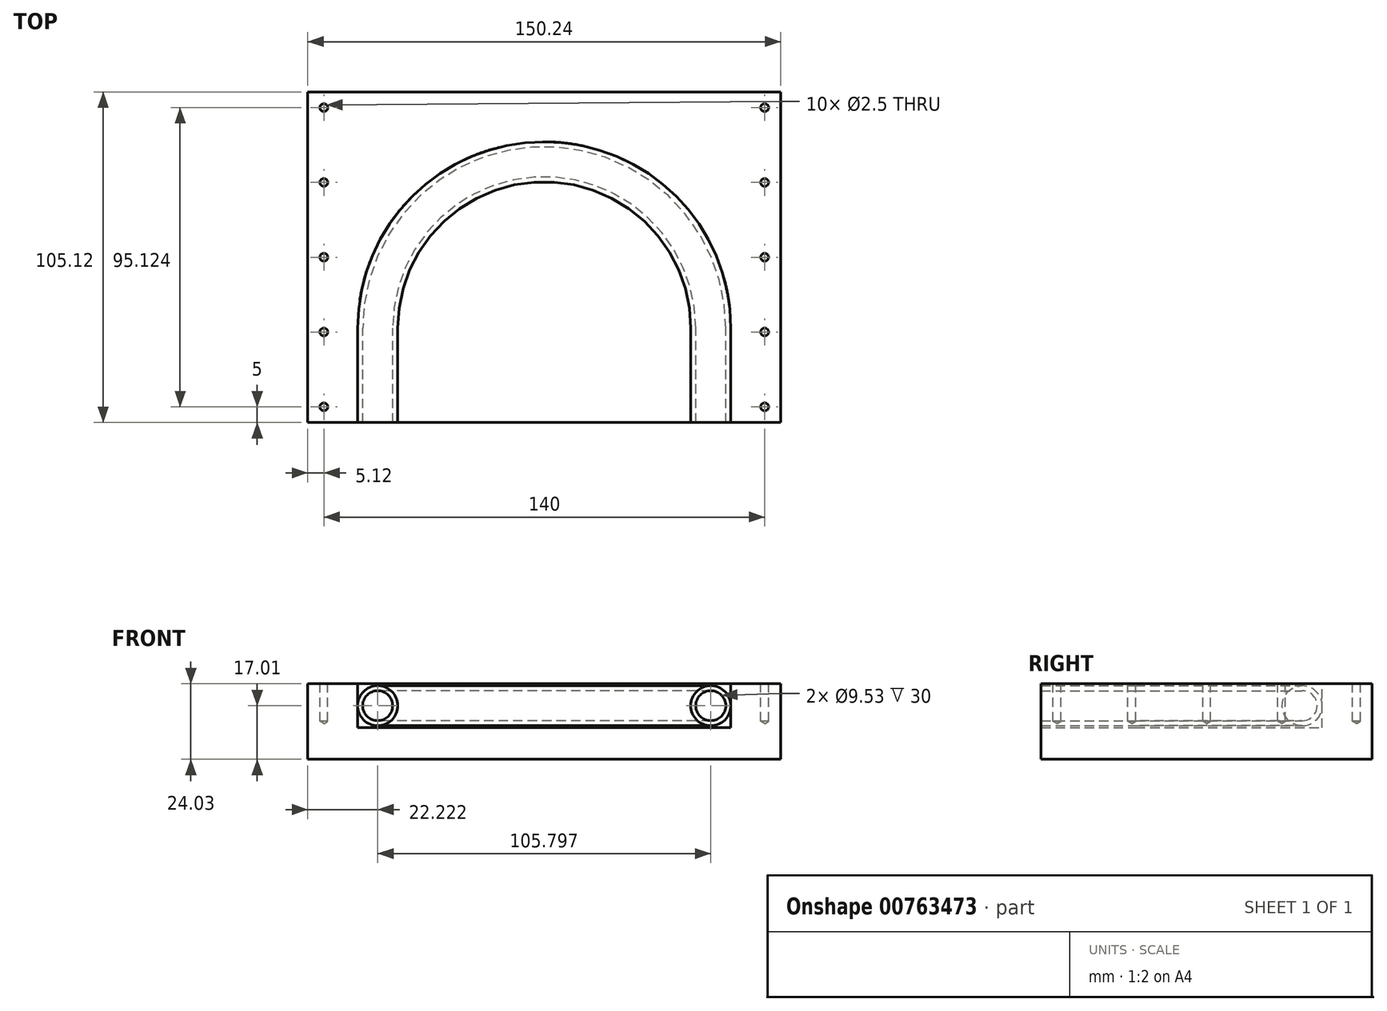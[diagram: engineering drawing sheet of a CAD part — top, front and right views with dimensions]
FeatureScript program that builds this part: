
annotation { "Feature Type Name" : "Feature", "Feature Type Description" : "" }
export const myFeature = defineFeature(function(context is Context, id is Id, definition is map)
    precondition{}
    {
        {
            var Q0;
            Q0=qCreatedBy(makeId("Right.planeOp"),FACE);
            var sketch = newSketch(context, id + "F0", { "sketchPlane" : qUnion([Q0])});
            skCircle(sketch, "E0", {"center": v(52.9, 0) * mm, "radius": 4.76 * mm});
            skCircle(sketch, "E1", {"center": v(52.9, 0) * mm, "radius": 6.35 * mm});
            skLineSegment(sketch, "E2", {"start": v(0, 42.85) * mm, "end": v(0, -34.67) * mm, "construction": true});
            skLineSegment(sketch, "E3.bottom", {"start": v(59.25, 7.01) * mm, "end": v(65.12, 7.01) * mm});
            skLineSegment(sketch, "E3.top", {"start": v(59.25, -7.01) * mm, "end": v(65.12, -7.01) * mm});
            skLineSegment(sketch, "E3.left", {"start": v(59.25, 7.01) * mm, "end": v(59.25, -7.01) * mm});
            skLineSegment(sketch, "E3.right", {"start": v(65.12, 7.01) * mm, "end": v(65.12, -7.01) * mm});
            skPoint(sketch, "E3.middle", {"position": v(62.19, 0) * mm});
            skPoint(sketch, "E4.visualSharp", {"position": v(59.25, 7.01) * mm});
            skPoint(sketch, "E5.visualSharp", {"position": v(65.12, 7.01) * mm});
            skLineSegment(sketch, "E6.bottom", {"start": v(65.12, -7.01) * mm, "end": v(-30, -7.01) * mm});
            skLineSegment(sketch, "E6.top", {"start": v(65.12, -17.01) * mm, "end": v(-30, -17.01) * mm});
            skLineSegment(sketch, "E6.left", {"start": v(65.12, -7.01) * mm, "end": v(65.12, -17.01) * mm});
            skLineSegment(sketch, "E6.right", {"start": v(-30, -7.01) * mm, "end": v(-30, -17.01) * mm});
            skSolve(sketch);
        }
        {
            var Q0;
            Q0=makeQuery(id+"F0.imprint","IMPRINT",FACE,{"disambiguationData":[TD([[makeQuery(id+"F0.imprint","IMPRINT",EDGE,{"derivedFrom":sQuery(id+"F0.wireOp",EDGE,"E0")}),-1.0]])]});
            var Q1;
            Q1=sQuery(id+"F0.wireOp",EDGE,"E2");
            revolve(context, id + "F1", {"surfaceOperationType" : NewSurfaceOperationType.NEW, "entities" : qUnion([Q0]), "axis" : qUnion([Q1]), "revolveType" : RevolveType.SYMMETRIC, "angle" : 180 * degree});
        }
        {
            var Q0;
            Q0=makeQuery(id+"F0.imprint","IMPRINT",FACE,{"disambiguationData":[TD([[makeQuery(id+"F0.imprint","IMPRINT",EDGE,{"derivedFrom":sQuery(id+"F0.wireOp",EDGE,"E3.bottom")}),-1.0]])]});
            var Q1;
            Q1=sQuery(id+"F0.wireOp",EDGE,"E2");
            revolve(context, id + "F2", {"operationType" : NewBodyOperationType.ADD, "surfaceOperationType" : NewSurfaceOperationType.NEW, "entities" : qUnion([Q0]), "axis" : qUnion([Q1]), "revolveType" : RevolveType.SYMMETRIC, "angle" : 180 * degree});
        }
        {
            var Q0;
            Q0=makeQuery(id+"F2.opRevolve","CAP_FACE",FACE,{"disambiguationData":[OSD([sQuery(id+"F0.wireOp",EDGE,"E3.bottom"),sQuery(id+"F0.wireOp",EDGE,"E3.top"),sQuery(id+"F0.wireOp",EDGE,"E3.left"),sQuery(id+"F0.wireOp",EDGE,"E3.right"),sQuery(id+"F0.wireOp",EDGE,"E4.filletArc"),sQuery(id+"F0.wireOp",EDGE,"E5.filletArc")])],"isStart":true});
            var Q1;
            Q1=makeQuery(id+"F2.opRevolve","CAP_FACE",FACE,{"disambiguationData":[OSD([sQuery(id+"F0.wireOp",EDGE,"E3.bottom"),sQuery(id+"F0.wireOp",EDGE,"E3.top"),sQuery(id+"F0.wireOp",EDGE,"E3.left"),sQuery(id+"F0.wireOp",EDGE,"E3.right"),sQuery(id+"F0.wireOp",EDGE,"E4.filletArc"),sQuery(id+"F0.wireOp",EDGE,"E5.filletArc")])],"isStart":false});
            extrude(context, id + "F3", {"entities" : qUnion([Q0, Q1]), "operationType" : NewBodyOperationType.ADD, "depth" : 30 * mm, "offsetDistance" : 25 * mm});
        }
        {
            var Q0;
            Q0=makeQuery(id+"F1.opRevolve","CAP_FACE",FACE,{"disambiguationData":[OSD([sQuery(id+"F0.wireOp",EDGE,"E0"),sQuery(id+"F0.wireOp",EDGE,"E1")])],"isStart":true});
            var Q1;
            Q1=makeQuery(id+"F1.opRevolve","CAP_FACE",FACE,{"disambiguationData":[OSD([sQuery(id+"F0.wireOp",EDGE,"E0"),sQuery(id+"F0.wireOp",EDGE,"E1")])],"isStart":false});
            extrude(context, id + "F4", {"entities" : qUnion([Q0, Q1]), "operationType" : NewBodyOperationType.ADD, "depth" : 30 * mm, "offsetDistance" : 25 * mm});
        }
        {
            var Q0;
            Q0=qCreatedBy(makeId("Top.planeOp"),FACE);
            var sketch = newSketch(context, id + "F5", { "sketchPlane" : qUnion([Q0])});
            skLineSegment(sketch, "E7.bottom", {"start": v(52.5, -3.17) * mm, "end": v(-52.5, -3.17) * mm});
            skLineSegment(sketch, "E7.top", {"start": v(52.5, 3.17) * mm, "end": v(-52.5, 3.17) * mm});
            skLineSegment(sketch, "E7.left", {"start": v(52.5, -3.18) * mm, "end": v(52.5, 3.18) * mm});
            skLineSegment(sketch, "E7.right", {"start": v(-52.5, -3.17) * mm, "end": v(-52.5, 3.17) * mm});
            skPoint(sketch, "E7.middle", {"position": v(0, 0) * mm});
            skArc(sketch, "E8", {"start": v(-52.5, 3.17) * mm, "mid": v(-55.67, 0) * mm, "end": v(-52.5, -3.17) * mm});
            skArc(sketch, "E9", {"start": v(52.5, -3.18) * mm, "mid": v(55.68, 0) * mm, "end": v(52.5, 3.18) * mm});
            skCircle(sketch, "E10", {"center": v(0, 0) * mm, "radius": 1.47 * mm});
            skSolve(sketch);
        }
        {
            var Q0;
            Q0=makeQuery(id+"F0.imprint","IMPRINT",FACE,{"disambiguationData":[TD([[makeQuery(id+"F0.imprint","IMPRINT",EDGE,{"derivedFrom":sQuery(id+"F0.wireOp",EDGE,"E6.top")}),-1.0]])]});
            extrude(context, id + "F6", {"entities" : qUnion([Q0]), "operationType" : NewBodyOperationType.ADD, "endBound" : BoundingType.SYMMETRIC, "depth" : 150.24 * mm, "offsetDistance" : 25 * mm});
        }
        {
            var Q0;
            Q0=makeQuery(id+"F5.imprint","IMPRINT",FACE,{"disambiguationData":[TD([[makeQuery(id+"F5.imprint","IMPRINT",EDGE,{"derivedFrom":sQuery(id+"F5.wireOp",EDGE,"E7.bottom")}),-1.0]])]});
            var Q1;
            {var subQ0=sQuery(id+"F5.wireOp",EDGE,"E7.left");Q1=makeQuery(id+"F5.imprint","IMPRINT",FACE,{"disambiguationData":[TD([[makeQuery(id+"F5.imprint","IMPRINT",EDGE,{"derivedFrom":subQ0}),-1.0]])]});}
            var Q2;
            {var subQ0=sQuery(id+"F5.wireOp",EDGE,"E7.left");Q2=makeQuery(id+"F5.imprint","IMPRINT",FACE,{"disambiguationData":[TD([[makeQuery(id+"F5.imprint","IMPRINT",EDGE,{"derivedFrom":subQ0}),1.0]])]});}
            var Q3;
            {var subQ0=sQuery(id+"F5.wireOp",EDGE,"E7.right");Q3=makeQuery(id+"F5.imprint","IMPRINT",FACE,{"disambiguationData":[TD([[makeQuery(id+"F5.imprint","IMPRINT",EDGE,{"derivedFrom":subQ0}),1.0]])]});}
            var Q4;
            {var subQ0=sQuery(id+"F5.wireOp",EDGE,"E7.right");Q4=makeQuery(id+"F5.imprint","IMPRINT",FACE,{"disambiguationData":[TD([[makeQuery(id+"F5.imprint","IMPRINT",EDGE,{"derivedFrom":subQ0}),-1.0]])]});}
            extrude(context, id + "F7", {"entities" : qUnion([Q0, Q1, Q2, Q3, Q4]), "endBound" : BoundingType.SYMMETRIC, "depth" : 12 * mm, "offsetDistance" : 25 * mm});
        }
        {
            var Q0;
            Q0=makeQuery(id+"F6.opExtrude","SWEPT_FACE",FACE,{"disambiguationData":[OSD([sQuery(id+"F0.wireOp",EDGE,"E6.left")])]});
            extrude(context, id + "F8", {"entities" : qUnion([Q0]), "operationType" : NewBodyOperationType.ADD, "depth" : 10 * mm, "offsetDistance" : 25 * mm});
        }
        {
            var Q0;
            {var subQ0=sQuery(id+"F0.wireOp",EDGE,"E6.left");var subQ1=sQuery(id+"F0.wireOp",EDGE,"E6.bottom");var subQ2=sQuery(id+"F0.wireOp",EDGE,"E3.right");var subQ3=makeQuery(id+"F6.opExtrude","SWEPT_FACE",FACE,{"disambiguationData":[OSD([subQ1])]});Q0=makeQuery(id+"F8.boolean.opBoolean","MERGE",FACE,{"derivedFrom":[makeQuery(id+"F6.boolean.opBoolean","SPLIT",FACE,{"disambiguationData":[TD([makeQuery(id+"F3.opExtrude","SWEPT_FACE",FACE,{"disambiguationData":[OSD([subQ2]),TDD([makeQuery(id+"F2.opRevolve","CAP_EDGE",EDGE,{"disambiguationData":[OSD([subQ2])],"isStart":true})])]})])],"derivedFrom":subQ3}),makeQuery(id+"F6.boolean.opBoolean","SPLIT",FACE,{"disambiguationData":[TD([makeQuery(id+"F3.opExtrude","SWEPT_FACE",FACE,{"disambiguationData":[OSD([subQ2]),TDD([makeQuery(id+"F2.opRevolve","CAP_EDGE",EDGE,{"disambiguationData":[OSD([subQ2])],"isStart":false})])]})])],"derivedFrom":subQ3}),makeQuery(id+"F8.opExtrude","SWEPT_FACE",FACE,{"disambiguationData":[OSD([subQ2,subQ1,subQ0])]})]});}
            extrude(context, id + "F9", {"entities" : qUnion([Q0]), "operationType" : NewBodyOperationType.ADD, "depth" : 14.03 * mm, "offsetDistance" : 25 * mm});
        }
        {
            var Q0;
            Q0=makeQuery(id+"F9.opExtrude","CAP_FACE",FACE,{"disambiguationData":[OSD([sQuery(id+"F0.wireOp",EDGE,"E3.right"),sQuery(id+"F0.wireOp",EDGE,"E6.bottom"),sQuery(id+"F0.wireOp",EDGE,"E6.left")])],"isStart":false});
            var sketch = newSketch(context, id + "F10", { "sketchPlane" : qUnion([Q0])});
            skCircle(sketch, "E11", {"center": v(-70, -25) * mm, "radius": 1.5 * mm});
            skCircle(sketch, "E12", {"center": v(70, -25) * mm, "radius": 1.5 * mm});
            skCircle(sketch, "E13", {"center": v(70, -1.22) * mm, "radius": 1.5 * mm});
            skCircle(sketch, "E14", {"center": v(70, 22.56) * mm, "radius": 1.5 * mm});
            skCircle(sketch, "E15", {"center": v(70, 46.34) * mm, "radius": 1.5 * mm});
            skCircle(sketch, "E16", {"center": v(70, 70.12) * mm, "radius": 1.5 * mm});
            skCircle(sketch, "E17", {"center": v(-70, -1.22) * mm, "radius": 1.5 * mm});
            skCircle(sketch, "E18", {"center": v(-70, 22.56) * mm, "radius": 1.5 * mm});
            skCircle(sketch, "E19", {"center": v(-70, 46.34) * mm, "radius": 1.5 * mm});
            skCircle(sketch, "E20", {"center": v(-70, 70.12) * mm, "radius": 1.5 * mm});
            skSolve(sketch);
        }
        {
            var Q0;
            Q0=sQuery(id+"F10.wireOp",VERTEX,"E15.center");
            var Q1;
            Q1=sQuery(id+"F10.wireOp",VERTEX,"E14.center");
            var Q2;
            Q2=sQuery(id+"F10.wireOp",VERTEX,"E13.center");
            var Q3;
            Q3=sQuery(id+"F10.wireOp",VERTEX,"E12.center");
            var Q4;
            Q4=sQuery(id+"F10.wireOp",VERTEX,"E11.center");
            var Q5;
            Q5=sQuery(id+"F10.wireOp",VERTEX,"E17.center");
            var Q6;
            Q6=sQuery(id+"F10.wireOp",VERTEX,"E18.center");
            var Q7;
            Q7=sQuery(id+"F10.wireOp",VERTEX,"E19.center");
            var Q8;
            Q8=sQuery(id+"F10.wireOp",VERTEX,"E20.center");
            var Q9;
            Q9=sQuery(id+"F10.wireOp",VERTEX,"E16.center");
            var Q10;
            Q10=makeQuery(id+"F2.opRevolve","SWEPT_BODY",BODY,{"disambiguationData":[OSD([sQuery(id+"F0.wireOp",EDGE,"E3.bottom"),sQuery(id+"F0.wireOp",EDGE,"E3.left"),sQuery(id+"F0.wireOp",EDGE,"E3.right"),sQuery(id+"F0.wireOp",EDGE,"E6.bottom")])]});
            hole(context, id + "F11", {"style" : HoleStyle.SIMPLE, "endStyle" : HoleEndStyle.BLIND, "holeDiameter" : 2.5 * mm, "majorDiameter" : 5 * mm, "holeDepth" : 12 * mm, "isTappedThrough" : true, "tappedDepth" : 12 * mm, "tapClearance" : 3, "locations" : qUnion([Q0, Q1, Q2, Q3, Q4, Q5, Q6, Q7, Q8, Q9]), "scope" : qUnion([Q10])});
        }
        {
            var Q0;
            Q0=makeQuery(id+"F7.opExtrude","SWEPT_BODY",BODY,{"disambiguationData":[OSD([sQuery(id+"F5.wireOp",EDGE,"E7.bottom"),sQuery(id+"F5.wireOp",EDGE,"E7.top"),sQuery(id+"F5.wireOp",EDGE,"E8"),sQuery(id+"F5.wireOp",EDGE,"E9"),sQuery(id+"F5.wireOp",EDGE,"E10")])]});
            deleteBodies(context, id + "F12", {"entities" : qUnion([Q0])});
        }
    });
